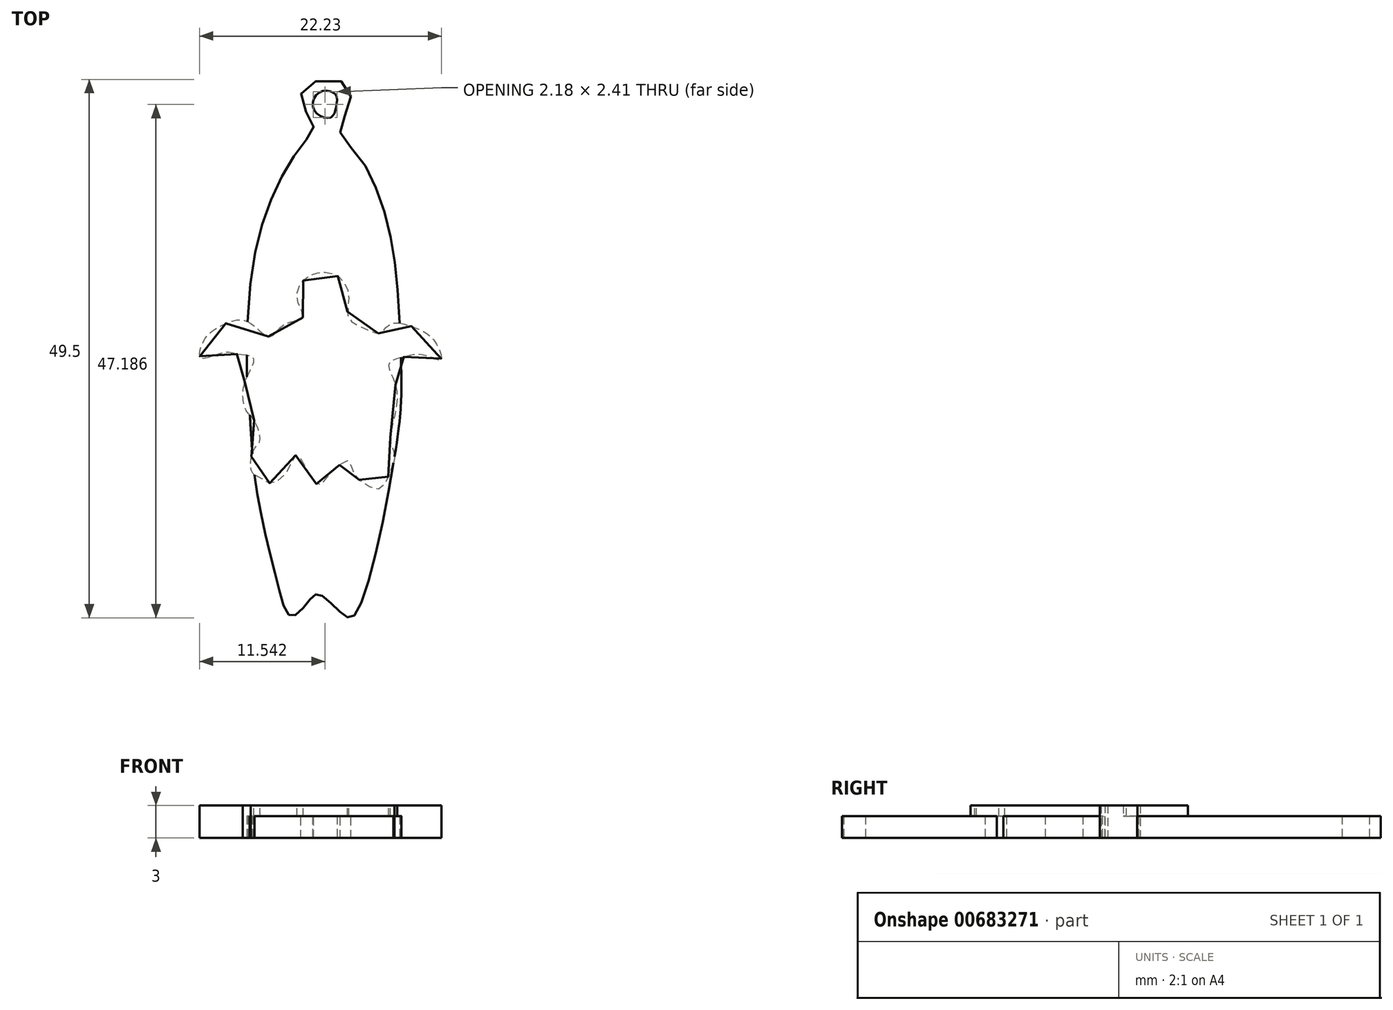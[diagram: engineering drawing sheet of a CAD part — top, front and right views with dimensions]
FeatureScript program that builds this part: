
annotation { "Feature Type Name" : "Feature", "Feature Type Description" : "" }
export const myFeature = defineFeature(function(context is Context, id is Id, definition is map)
    precondition{}
    {
        {
            var Q0;
            Q0=qCreatedBy(makeId("Top.planeOp"),FACE);
            var sketch = newSketch(context, id + "F0", { "sketchPlane" : qUnion([Q0])});
            skFitSpline(sketch, "E0", {"points": [v(-43.25, 51.43) * mm, v(-44.17, 53.32) * mm, v(-43.98, 55.25) * mm, v(-40.3, 55.48) * mm, v(-40.07, 53.13) * mm, v(-40.8, 51.1) * mm, v(-39.24, 48.95) * mm, v(-37.4, 45.63) * mm, v(-36.12, 41.17) * mm, v(-35.52, 36.43) * mm, v(-35.2, 29.35) * mm, v(-35.2, 26.45) * mm, v(-35.75, 21.48) * mm, v(-39.5, 6.58) * mm, v(-40.6, 6.72) * mm, v(-42.74, 8.51) * mm, v(-43.57, 8.03) * mm, v(-45.22, 6.51) * mm, v(-46.6, 9.68) * mm, v(-48.53, 18.44) * mm, v(-49.08, 24.7) * mm, v(-49.36, 28.5) * mm, v(-49.01, 37.25) * mm, v(-47.77, 43.11) * mm, v(-45.98, 47.25) * mm, v(-44.12, 50.07) * mm, v(-43.25, 51.43) * mm]});
            skFitSpline(sketch, "E1", {"points": [v(-41.15, 53.38) * mm, v(-41.7, 52.35) * mm, v(-43.22, 53.1) * mm, v(-42.67, 54.69) * mm, v(-41.22, 54.48) * mm, v(-41.15, 53.38) * mm]});
            skSolve(sketch);
        }
        {
            var Q0;
            Q0=makeQuery(id+"F0.imprint","IMPRINT",FACE,{"disambiguationData":[TD([[makeQuery(id+"F0.imprint","IMPRINT",EDGE,{"derivedFrom":sQuery(id+"F0.wireOp",EDGE,"E0")}),-1.0]])]});
            extrude(context, id + "F1", {"entities" : qUnion([Q0]), "depth" : 2 * mm, "offsetDistance" : 25 * mm});
        }
        {
            var Q0;
            Q0=qCreatedBy(makeId("Top.planeOp"),FACE);
            var sketch = newSketch(context, id + "F2", { "sketchPlane" : qUnion([Q0])});
            skFitSpline(sketch, "E2", {"points": [v(-44.2, 33.97) * mm, v(-44.72, 35.55) * mm, v(-44.35, 37.17) * mm, v(-43.17, 38) * mm, v(-41.55, 38.03) * mm, v(-40.45, 37.2) * mm, v(-40, 35.7) * mm, v(-40, 33.9) * mm, v(-38.38, 32.9) * mm, v(-37.04, 32.56) * mm, v(-36.25, 33.38) * mm, v(-34.28, 33.18) * mm, v(-32.18, 31.87) * mm, v(-31.56, 30.1) * mm, v(-33, 30.49) * mm, v(-34.9, 30.35) * mm, v(-36.32, 29.7) * mm, v(-35.87, 28.25) * mm, v(-35.63, 25.8) * mm, v(-36.18, 22.53) * mm, v(-35.8, 21.32) * mm, v(-36.45, 19.15) * mm, v(-37.25, 18.19) * mm, v(-38.87, 18.88) * mm, v(-39.66, 19.94) * mm, v(-40.04, 20.77) * mm, v(-41.18, 20.15) * mm, v(-42.31, 18.9) * mm, v(-42.62, 18.56) * mm, v(-43.17, 18.84) * mm, v(-44.14, 20.53) * mm, v(-44.83, 21.32) * mm, v(-45.55, 20.01) * mm, v(-47.07, 18.7) * mm, v(-47.93, 19.12) * mm, v(-48.9, 19.77) * mm, v(-48.69, 21.87) * mm, v(-48.17, 22.63) * mm, v(-48.8, 24.66) * mm, v(-49.41, 25.39) * mm, v(-49.58, 27.9) * mm, v(-48.76, 30.21) * mm, v(-50.2, 30.6) * mm, v(-51.58, 30.73) * mm, v(-53.58, 30.25) * mm, v(-53.27, 31.94) * mm, v(-51.62, 33.28) * mm, v(-49.34, 33.62) * mm, v(-47.3, 32.21) * mm, v(-45.9, 33.35) * mm, v(-44.2, 33.97) * mm]});
            skSolve(sketch);
        }
        {
            var Q0;
            Q0 = qSketchRegion(id + "F2", true);
            extrude(context, id + "F3", {"entities" : qUnion([Q0]), "operationType" : NewBodyOperationType.ADD, "depth" : 3 * mm, "offsetDistance" : 25 * mm});
        }
        {
            var Q0;
            Q0=qCreatedBy(makeId("Top.planeOp"),FACE);
            var sketch = newSketch(context, id + "F4", { "sketchPlane" : qUnion([Q0])});
            skFitSpline(sketch, "E3", {"points": [v(-42.36, 32.92) * mm, v(-43.48, 34.38) * mm, v(-43.73, 36.18) * mm, v(-42.75, 37.2) * mm, v(-41.2, 36.38) * mm, v(-40.9, 34.86) * mm, v(-42.36, 32.92) * mm]});
            skSolve(sketch);
        }
        {
            var Q0;
            Q0 = qSketchRegion(id + "F4", true);
            extrude(context, id + "F5", {"entities" : qUnion([Q0]), "operationType" : NewBodyOperationType.ADD, "depth" : 1 * mm, "offsetDistance" : 25 * mm});
        }
    });
